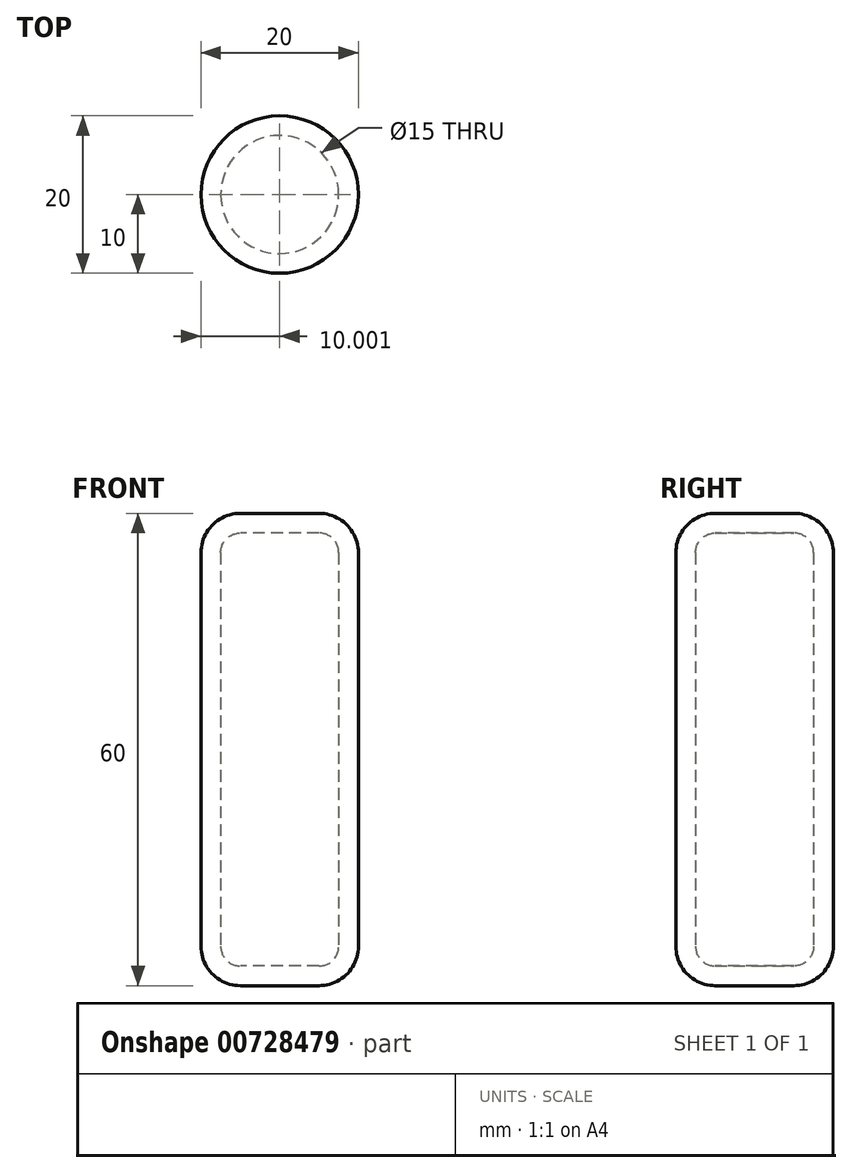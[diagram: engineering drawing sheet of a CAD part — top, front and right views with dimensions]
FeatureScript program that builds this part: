
annotation { "Feature Type Name" : "Feature", "Feature Type Description" : "" }
export const myFeature = defineFeature(function(context is Context, id is Id, definition is map)
    precondition{}
    {
        {
            var Q0;
            Q0=qCreatedBy(makeId("Top.planeOp"),FACE);
            var sketch = newSketch(context, id + "F0", { "sketchPlane" : qUnion([Q0])});
            skCircle(sketch, "E0", {"center": v(-2.78, 0.25) * mm, "radius": 10 * mm});
            skSolve(sketch);
        }
        {
            var Q0;
            Q0=makeQuery(id+"F0.imprint","IMPRINT",FACE,{"disambiguationData":[TD([[makeQuery(id+"F0.imprint","IMPRINT",EDGE,{"derivedFrom":sQuery(id+"F0.wireOp",EDGE,"E0")}),1.0]])]});
            extrude(context, id + "F1", {"entities" : qUnion([Q0]), "endBound" : BoundingType.SYMMETRIC, "depth" : 60 * mm, "offsetDistance" : 25 * mm});
        }
        {
            var Q0;
            Q0=makeQuery(id+"F1.opExtrude","CAP_EDGE",EDGE,{"disambiguationData":[OSD([sQuery(id+"F0.wireOp",EDGE,"E0")])],"isStart":false});
            fillet(context, id + "F2", {"entities" : qUnion([Q0]), "tangentPropagation" : true, "radius" : 5 * mm, "defaultsChanged" : false, "vertexSettings" : [], "allowEdgeOverflow" : false});
        }
        {
            var Q0;
            Q0=makeQuery(id+"F1.opExtrude","CAP_EDGE",EDGE,{"disambiguationData":[OSD([sQuery(id+"F0.wireOp",EDGE,"E0")])],"isStart":true});
            fillet(context, id + "F3", {"entities" : qUnion([Q0]), "tangentPropagation" : true, "radius" : 5 * mm, "defaultsChanged" : false, "vertexSettings" : [], "allowEdgeOverflow" : false});
        }
        {
            var Q0;
            Q0=makeQuery(id+"F1.opExtrude","SWEPT_FACE",FACE,{"disambiguationData":[OSD([sQuery(id+"F0.wireOp",EDGE,"E0")])]});
            var Q1;
            Q1=makeQuery(id+"F2.opFillet","BLEND_FACE",FACE,{"disambiguationData":[OSD([sQuery(id+"F0.wireOp",EDGE,"E0")])]});
            var Q2;
            Q2=makeQuery(id+"F1.opExtrude","CAP_FACE",FACE,{"disambiguationData":[OSD([sQuery(id+"F0.wireOp",EDGE,"E0")])],"isStart":false});
            var Q3;
            Q3=makeQuery(id+"F1.opExtrude","SWEPT_BODY",BODY,{"disambiguationData":[OSD([sQuery(id+"F0.wireOp",EDGE,"E0")])]});
            shell(context, id + "F4", {"isHollow" : true, "entities" : qUnion([Q0, Q1, Q2]), "parts" : qUnion([Q3]), "thickness" : 2.5 * mm});
        }
        {
            var Q0;
            Q0=qCreatedBy(makeId("Front.planeOp"),FACE);
            var sketch = newSketch(context, id + "F5", { "sketchPlane" : qUnion([Q0])});
            skLineSegment(sketch, "E1.bottom", {"start": v(11.58, 60.82) * mm, "end": v(-18.42, 60.82) * mm});
            skLineSegment(sketch, "E1.top", {"start": v(11.58, 35.82) * mm, "end": v(-18.42, 35.82) * mm});
            skLineSegment(sketch, "E1.left", {"start": v(11.58, 60.82) * mm, "end": v(11.58, 35.82) * mm});
            skLineSegment(sketch, "E1.right", {"start": v(-18.42, 60.82) * mm, "end": v(-18.42, 35.82) * mm});
            skSolve(sketch);
        }
        {
            var Q0;
            Q0=sQuery(id+"F5.wireOp",EDGE,"E1.bottom");
            var Q1;
            Q1=sQuery(id+"F5.wireOp",EDGE,"E1.right");
            var Q2;
            Q2=sQuery(id+"F5.wireOp",EDGE,"E1.top");
            var Q3;
            Q3=sQuery(id+"F5.wireOp",EDGE,"E1.left");
            extrude(context, id + "F6", {"bodyType" : ToolBodyType.SURFACE, "surfaceEntities" : qUnion([Q0, Q1, Q2, Q3]), "endBound" : BoundingType.SYMMETRIC, "depth" : 50 * mm, "offsetDistance" : 25 * mm});
        }
    });
